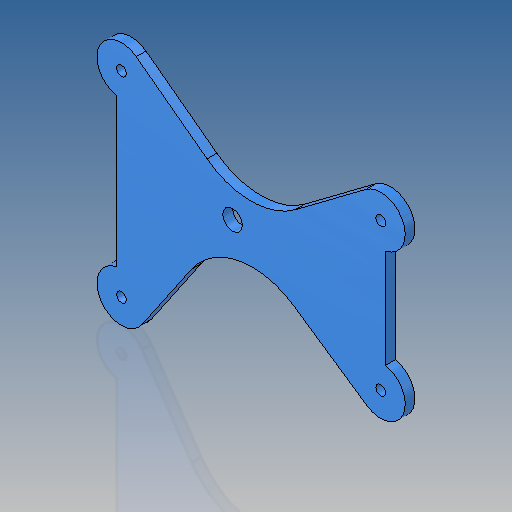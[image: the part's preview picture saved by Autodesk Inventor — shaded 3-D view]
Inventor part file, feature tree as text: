
AUTODESK INVENTOR PART (.ipt)
format: ipt  version: 2017 (Build 210142000, 142)  size: 139,264 bytes
history: native  units: mm
features: other x4, reference x4, extrude x1, sketch x1
ambient origin geometry x8: Origin, YZ Plane, XZ Plane, XY Plane, X Axis, Y Axis, Z Axis, Center Point
bodies: Body1 (feature_tree)
feature tree (10):
  other  "Sólido1"
  extrude  "Extrusión1"  Depth=30.0mm
  sketch  "Boceto1"  dims[d0=10.0mm d1=8.0mm d2=4.0mm d3=0.0mm d4=10.0mm d5=30.0mm d6=8.0mm d7=90.0deg]
  reference  "Referencia1"
  reference  "Referencia2"
  reference  "Referencia3"
  reference  "Referencia5"
  other  "<userpath>\Documents\GitHub\actor-re-actor\models\inventor-caja\Case\CaseB.iam"
  other  "CaseB.iam"
  other  "CaseB:1"
